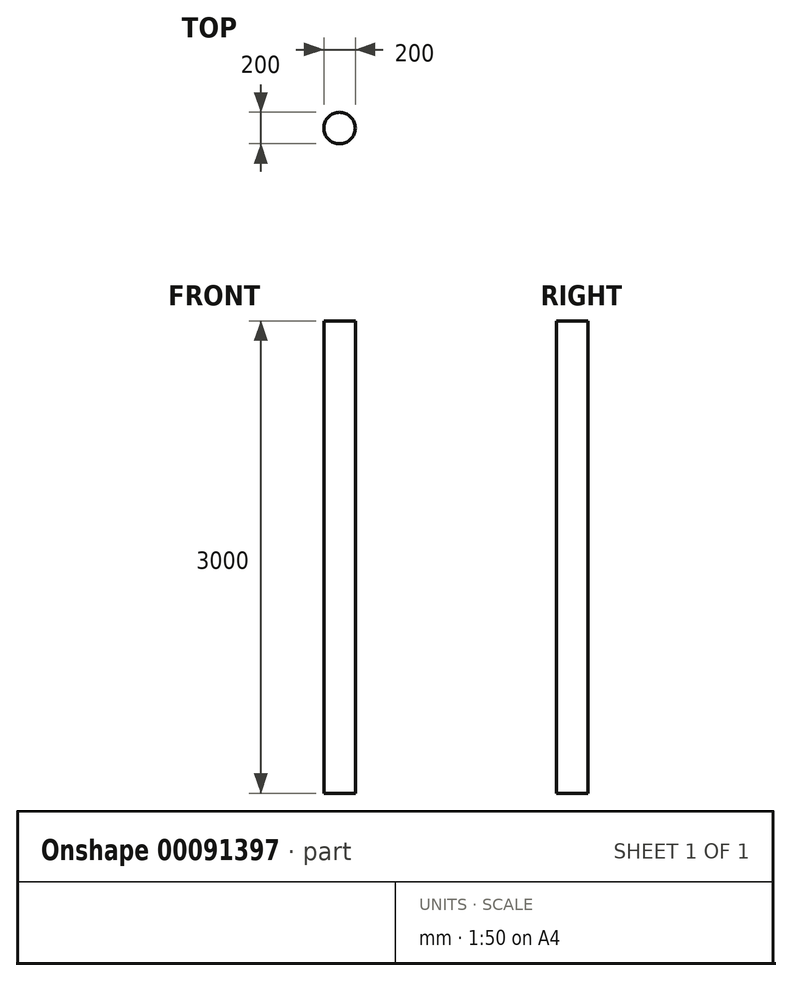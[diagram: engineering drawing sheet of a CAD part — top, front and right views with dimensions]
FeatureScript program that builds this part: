
annotation { "Feature Type Name" : "Feature", "Feature Type Description" : "" }
export const myFeature = defineFeature(function(context is Context, id is Id, definition is map)
    precondition{}
    {
        {
            var Q0;
            Q0=qCreatedBy(makeId("Top.planeOp"),FACE);
            var sketch = newSketch(context, id + "F0", { "sketchPlane" : qUnion([Q0])});
            skCircle(sketch, "E0", {"center": v(0, 0) * mm, "radius": 100 * mm});
            skSolve(sketch);
        }
        {
            var Q0;
            Q0 = qSketchRegion(id + "F0", true);
            extrude(context, id + "F1", {"entities" : qUnion([Q0]), "depth" : 3000 * mm});
        }
    });
